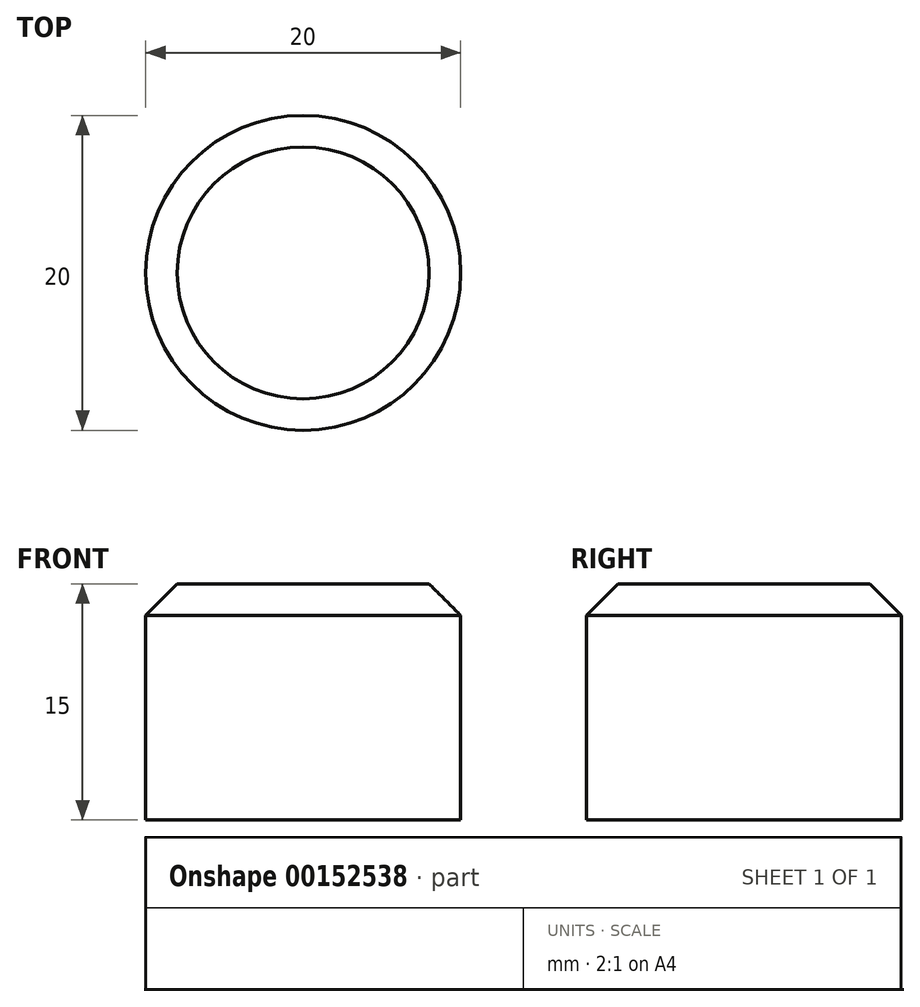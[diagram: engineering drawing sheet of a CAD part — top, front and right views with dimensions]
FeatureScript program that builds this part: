
annotation { "Feature Type Name" : "Feature", "Feature Type Description" : "" }
export const myFeature = defineFeature(function(context is Context, id is Id, definition is map)
    precondition{}
    {
        {
            var Q0;
            Q0=qCreatedBy(makeId("Top.planeOp"),FACE);
            var sketch = newSketch(context, id + "F0", { "sketchPlane" : qUnion([Q0])});
            skCircle(sketch, "E0", {"center": v(-42.62, 50.85) * mm, "radius": 10 * mm});
            skSolve(sketch);
        }
        {
            var Q0;
            Q0=makeQuery(id+"F0.imprint","IMPRINT",FACE,{"disambiguationData":[TD([[makeQuery(id+"F0.imprint","IMPRINT",EDGE,{"derivedFrom":sQuery(id+"F0.wireOp",EDGE,"E0")}),1.0]])]});
            extrude(context, id + "F1", {"entities" : qUnion([Q0]), "depth" : 15 * mm});
        }
        {
            var Q0;
            Q0=makeQuery(id+"F1.opExtrude","CAP_FACE",FACE,{"disambiguationData":[OSD([sQuery(id+"F0.wireOp",EDGE,"E0")])],"isStart":false});
            chamfer(context, id + "F2", {"entities" : qUnion([Q0]), "width" : 2 * mm, "tangentPropagation" : true});
        }
    });
